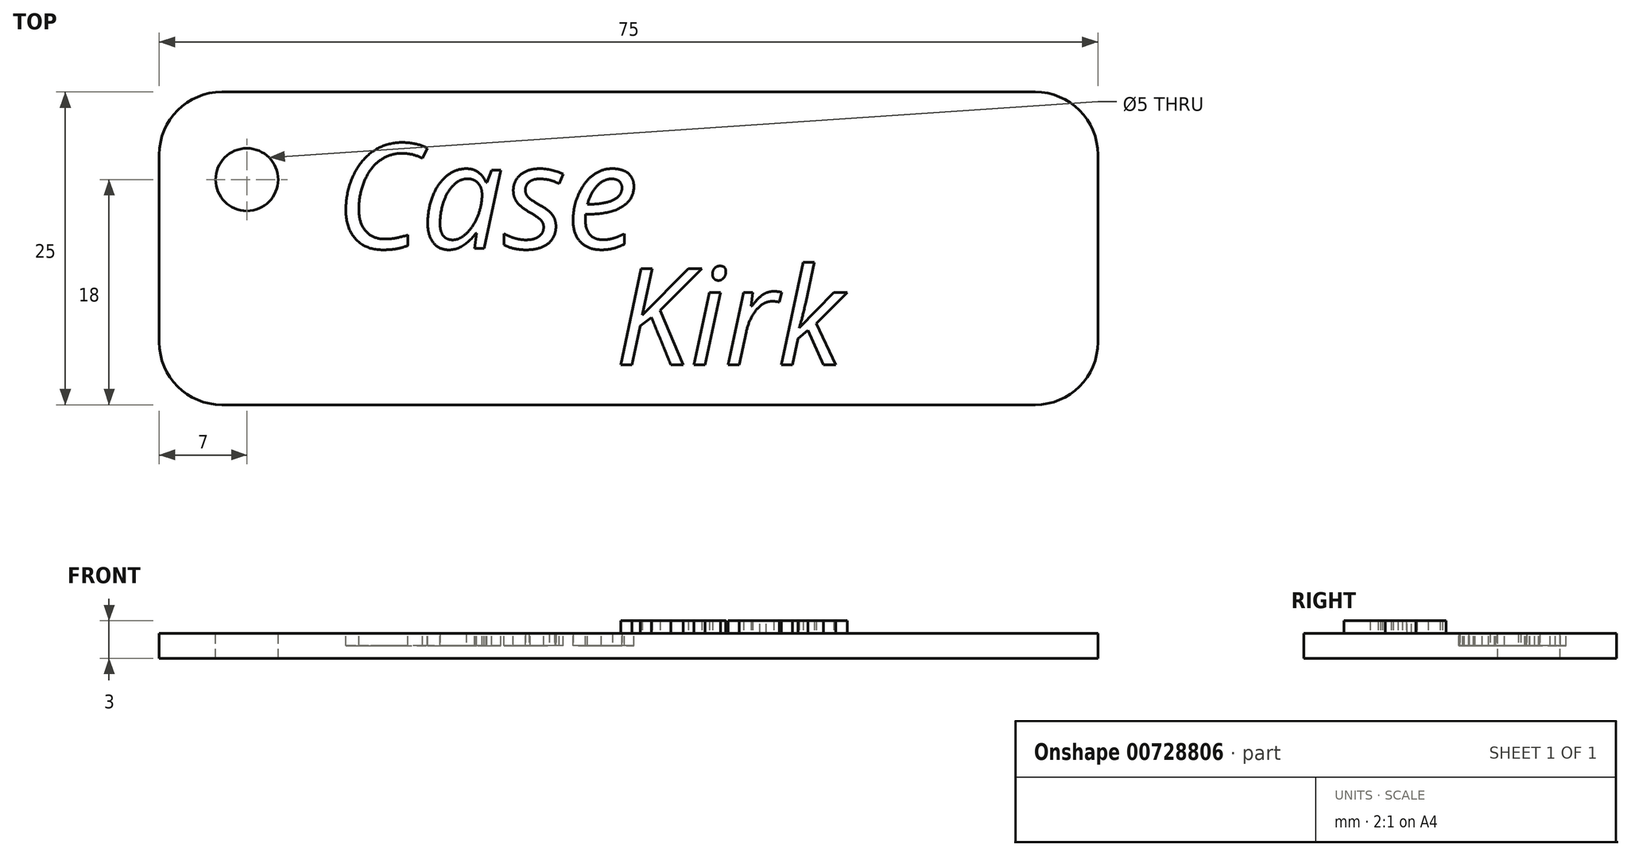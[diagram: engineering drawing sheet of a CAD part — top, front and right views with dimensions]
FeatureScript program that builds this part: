
annotation { "Feature Type Name" : "Feature", "Feature Type Description" : "" }
export const myFeature = defineFeature(function(context is Context, id is Id, definition is map)
    precondition{}
    {
        {
            var Q0;
            Q0=qCreatedBy(makeId("Top.planeOp"),FACE);
            var sketch = newSketch(context, id + "F0", { "sketchPlane" : qUnion([Q0])});
            skLineSegment(sketch, "E0.bottom", {"start": v(32.5, 12.5) * mm, "end": v(-32.5, 12.5) * mm});
            skLineSegment(sketch, "E0.top", {"start": v(32.5, -12.5) * mm, "end": v(-32.5, -12.5) * mm});
            skLineSegment(sketch, "E0.left", {"start": v(37.5, 7.5) * mm, "end": v(37.5, -7.5) * mm});
            skLineSegment(sketch, "E0.right", {"start": v(-37.5, 7.5) * mm, "end": v(-37.5, -7.5) * mm});
            skPoint(sketch, "E0.middle", {"position": v(0, 0) * mm});
            skPoint(sketch, "E1.visualSharp", {"position": v(-37.5, 12.5) * mm});
            skArc(sketch, "E1.filletArc", {"start": v(-32.5, 12.5) * mm, "mid": v(-36.04, 11.04) * mm, "end": v(-37.5, 7.5) * mm});
            skPoint(sketch, "E2.visualSharp", {"position": v(37.5, 12.5) * mm});
            skArc(sketch, "E2.filletArc", {"start": v(37.5, 7.5) * mm, "mid": v(36.04, 11.04) * mm, "end": v(32.5, 12.5) * mm});
            skPoint(sketch, "E3.visualSharp", {"position": v(37.5, -12.5) * mm});
            skArc(sketch, "E3.filletArc", {"start": v(32.5, -12.5) * mm, "mid": v(36.04, -11.04) * mm, "end": v(37.5, -7.5) * mm});
            skPoint(sketch, "E4.visualSharp", {"position": v(-37.5, -12.5) * mm});
            skArc(sketch, "E4.filletArc", {"start": v(-37.5, -7.5) * mm, "mid": v(-36.04, -11.04) * mm, "end": v(-32.5, -12.5) * mm});
            skSolve(sketch);
        }
        {
            var Q0;
            Q0=makeQuery(id+"F0.imprint","IMPRINT",FACE,{"disambiguationData":[TD([[makeQuery(id+"F0.imprint","IMPRINT",EDGE,{"derivedFrom":sQuery(id+"F0.wireOp",EDGE,"E0.bottom")}),1.0]])]});
            extrude(context, id + "F1", {"entities" : qUnion([Q0]), "depth" : 2 * mm, "offsetDistance" : 25 * mm});
        }
        {
            var Q0;
            Q0=makeQuery(id+"F1.opExtrude","CAP_FACE",FACE,{"disambiguationData":[OSD([sQuery(id+"F0.wireOp",EDGE,"E0.bottom"),sQuery(id+"F0.wireOp",EDGE,"E0.top"),sQuery(id+"F0.wireOp",EDGE,"E0.left"),sQuery(id+"F0.wireOp",EDGE,"E0.right"),sQuery(id+"F0.wireOp",EDGE,"E1.filletArc"),sQuery(id+"F0.wireOp",EDGE,"E2.filletArc"),sQuery(id+"F0.wireOp",EDGE,"E3.filletArc"),sQuery(id+"F0.wireOp",EDGE,"E4.filletArc")])],"isStart":false});
            var sketch = newSketch(context, id + "F2", { "sketchPlane" : qUnion([Q0])});
            skPoint(sketch, "E5", {"position": v(-30.5, 5.5) * mm});
            skSolve(sketch);
        }
        {
            var Q0;
            Q0=sQuery(id+"F2.wireOp",VERTEX,"E5");
            var Q1;
            Q1=makeQuery(id+"F1.opExtrude","SWEPT_BODY",BODY,{"disambiguationData":[OSD([sQuery(id+"F0.wireOp",EDGE,"E0.bottom"),sQuery(id+"F0.wireOp",EDGE,"E0.top"),sQuery(id+"F0.wireOp",EDGE,"E0.left"),sQuery(id+"F0.wireOp",EDGE,"E0.right"),sQuery(id+"F0.wireOp",EDGE,"E1.filletArc"),sQuery(id+"F0.wireOp",EDGE,"E2.filletArc"),sQuery(id+"F0.wireOp",EDGE,"E3.filletArc"),sQuery(id+"F0.wireOp",EDGE,"E4.filletArc")])]});
            hole(context, id + "F3", {"style" : HoleStyle.SIMPLE, "endStyle" : HoleEndStyle.THROUGH, "holeDiameter" : 5 * mm, "majorDiameter" : 5 * mm, "isTappedThrough" : true, "tappedDepth" : 12 * mm, "tapClearance" : 3, "locations" : qUnion([Q0]), "scope" : qUnion([Q1])});
        }
        {
            var Q0;
            Q0=makeQuery(id+"F1.opExtrude","CAP_FACE",FACE,{"disambiguationData":[OSD([sQuery(id+"F0.wireOp",EDGE,"E0.bottom"),sQuery(id+"F0.wireOp",EDGE,"E0.top"),sQuery(id+"F0.wireOp",EDGE,"E0.left"),sQuery(id+"F0.wireOp",EDGE,"E0.right"),sQuery(id+"F0.wireOp",EDGE,"E1.filletArc"),sQuery(id+"F0.wireOp",EDGE,"E2.filletArc"),sQuery(id+"F0.wireOp",EDGE,"E3.filletArc"),sQuery(id+"F0.wireOp",EDGE,"E4.filletArc")])],"isStart":false});
            var sketch = newSketch(context, id + "F4", { "sketchPlane" : qUnion([Q0])});
            skText(sketch, "E6", { "text": "Case", "fontName": "OpenSans-Italic.ttf"});
            const initialGuessF4  = {"E6": [-0.02345, 0, 1, 0, 0.00842]};
            skSetInitialGuess(sketch, initialGuessF4);
            skSolve(sketch);
        }
        {
            var Q0;
            Q0 = qSketchRegion(id + "F4", true);
            extrude(context, id + "F5", {"entities" : qUnion([Q0]), "operationType" : NewBodyOperationType.REMOVE, "oppositeDirection" : true, "depth" : 1 * mm, "offsetDistance" : 25 * mm});
        }
        {
            var Q0;
            {var subQ0=sQuery(id+"F0.wireOp",EDGE,"E4.filletArc");var subQ1=sQuery(id+"F0.wireOp",EDGE,"E3.filletArc");var subQ2=sQuery(id+"F0.wireOp",EDGE,"E2.filletArc");var subQ3=sQuery(id+"F0.wireOp",EDGE,"E1.filletArc");var subQ4=sQuery(id+"F0.wireOp",EDGE,"E0.bottom");var subQ5=sQuery(id+"F0.wireOp",EDGE,"E0.right");var subQ6=sQuery(id+"F0.wireOp",EDGE,"E0.top");var subQ7=sQuery(id+"F0.wireOp",EDGE,"E0.left");Q0=makeQuery(id+"F5.boolean.opBoolean","SPLIT",FACE,{"disambiguationData":[TD([makeQuery(id+"F1.opExtrude","SWEPT_FACE",FACE,{"disambiguationData":[OSD([subQ4])]})])],"derivedFrom":makeQuery(id+"F1.opExtrude","CAP_FACE",FACE,{"disambiguationData":[OSD([subQ4,subQ6,subQ7,subQ5,subQ3,subQ2,subQ1,subQ0])],"isStart":false})});}
            var sketch = newSketch(context, id + "F6", { "sketchPlane" : qUnion([Q0])});
            skText(sketch, "E7", { "text": "Kirk", "fontName": "OpenSans-Italic.ttf"});
            const initialGuessF6  = {"E7": [-0.00108, -0.0093, 1, 0, 0.00775]};
            skSetInitialGuess(sketch, initialGuessF6);
            skSolve(sketch);
        }
        {
            var Q0;
            Q0 = qSketchRegion(id + "F6", true);
            extrude(context, id + "F7", {"entities" : qUnion([Q0]), "operationType" : NewBodyOperationType.ADD, "depth" : 1 * mm, "offsetDistance" : 25 * mm});
        }
    });
